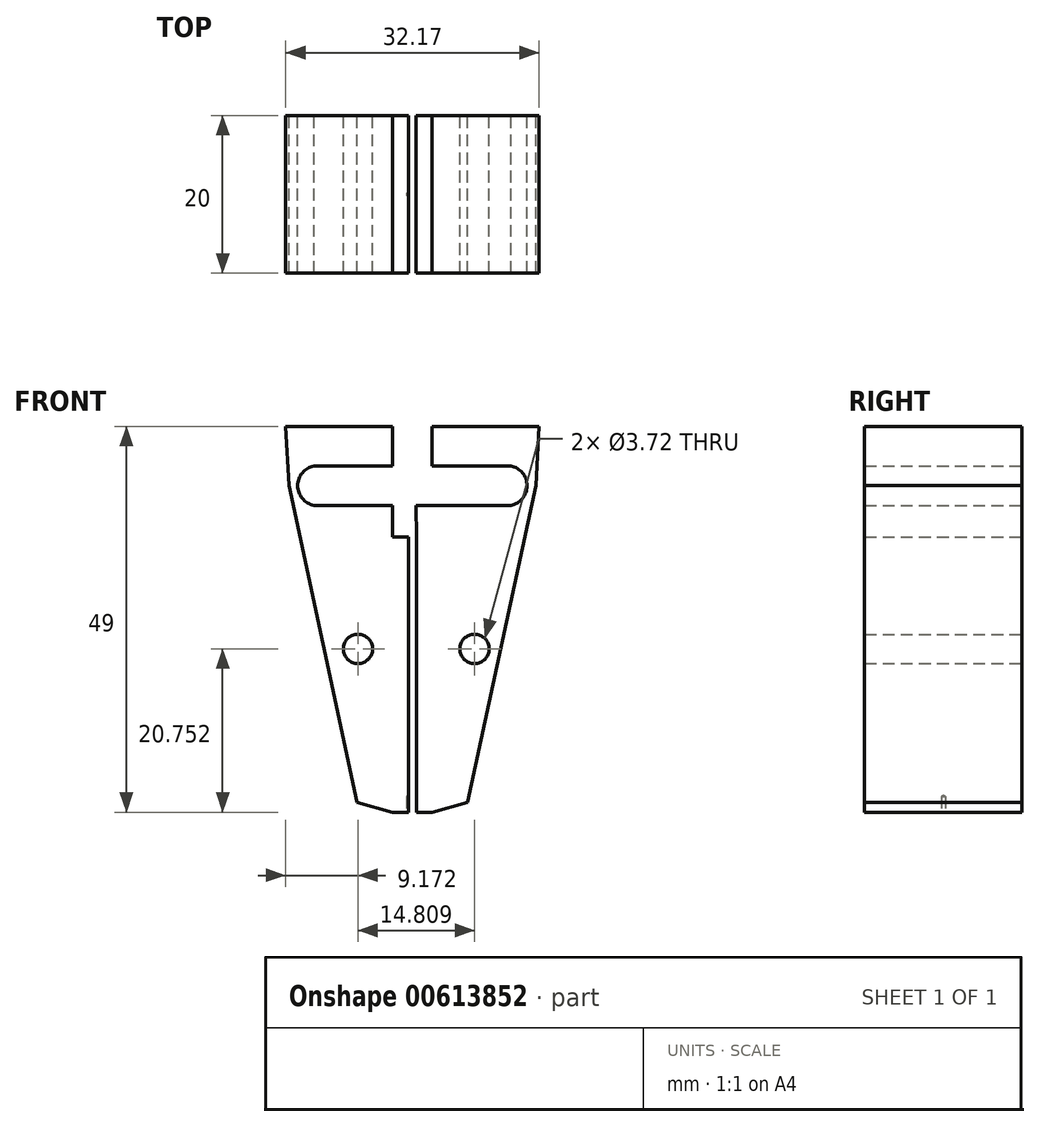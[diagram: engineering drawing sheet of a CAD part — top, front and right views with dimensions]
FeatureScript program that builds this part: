
annotation { "Feature Type Name" : "Feature", "Feature Type Description" : "" }
export const myFeature = defineFeature(function(context is Context, id is Id, definition is map)
    precondition{}
    {
        {
            var Q0;
            Q0=qCreatedBy(makeId("Front.planeOp"),FACE);
            var sketch = newSketch(context, id + "F0", { "sketchPlane" : qUnion([Q0])});
            skLineSegment(sketch, "E0.MirrorCS", {"start": v(38.69, 62.48) * mm, "end": v(39.08, 69.98) * mm});
            skLineSegment(sketch, "E1.MirrorCS", {"start": v(30.03, 22.23) * mm, "end": v(38.69, 62.48) * mm});
            skLineSegment(sketch, "E2.MirrorCS", {"start": v(25.5, 20.98) * mm, "end": v(30.03, 22.23) * mm});
            skLineSegment(sketch, "E3.MirrorCS", {"start": v(25.5, 64.98) * mm, "end": v(25.5, 69.98) * mm});
            skLineSegment(sketch, "E4.MirrorCS", {"start": v(35.5, 64.98) * mm, "end": v(25.5, 64.98) * mm});
            skArc(sketch, "E5.MirrorCS", {"start": v(35.5, 64.98) * mm, "mid": v(37.56, 62.48) * mm, "end": v(35.5, 59.98) * mm});
            skLineSegment(sketch, "E6.MirrorCS", {"start": v(25.5, 59.98) * mm, "end": v(35.5, 59.98) * mm});
            skLineSegment(sketch, "E7.MirrorCS", {"start": v(25.5, 20.98) * mm, "end": v(25.5, 55.9) * mm});
            skLineSegment(sketch, "E8", {"start": v(25.5, 69.98) * mm, "end": v(39.08, 69.98) * mm});
            skLineSegment(sketch, "E9.MirrorCS", {"start": v(20.5, 20.98) * mm, "end": v(20.5, 55.98) * mm});
            skLineSegment(sketch, "E10.MirrorCS", {"start": v(20.5, 59.98) * mm, "end": v(10.5, 59.98) * mm});
            skArc(sketch, "E11.MirrorCS", {"start": v(10.5, 64.98) * mm, "mid": v(8.43, 62.48) * mm, "end": v(10.5, 59.98) * mm});
            skLineSegment(sketch, "E12.MirrorCS", {"start": v(10.5, 64.98) * mm, "end": v(20.5, 64.98) * mm});
            skLineSegment(sketch, "E13.MirrorCS", {"start": v(20.5, 64.98) * mm, "end": v(20.5, 69.98) * mm});
            skLineSegment(sketch, "E14.MirrorCS", {"start": v(20.5, 69.98) * mm, "end": v(6.91, 69.98) * mm});
            skLineSegment(sketch, "E15.MirrorCS", {"start": v(7.3, 62.48) * mm, "end": v(6.91, 69.98) * mm});
            skLineSegment(sketch, "E16.MirrorCS", {"start": v(15.97, 22.23) * mm, "end": v(7.3, 62.48) * mm});
            skLineSegment(sketch, "E17.MirrorCS", {"start": v(20.5, 20.98) * mm, "end": v(15.97, 22.23) * mm});
            skLineSegment(sketch, "E18", {"start": v(10.98, 62.48) * mm, "end": v(35.02, 62.48) * mm, "construction": true});
            skLineSegment(sketch, "E19", {"start": v(74.89, 62.48) * mm, "end": v(35.02, 62.48) * mm, "construction": true});
            skLineSegment(sketch, "E20", {"start": v(10.98, 62.48) * mm, "end": v(-13.58, 62.48) * mm, "construction": true});
            skLineSegment(sketch, "E21.direction2", {"start": v(20.5, 22.1) * mm, "end": v(20.5, 24.4) * mm, "construction": true});
            skLineSegment(sketch, "E22", {"start": v(20.5, 64.98) * mm, "end": v(20.5, 59.98) * mm, "construction": true});
            skLineSegment(sketch, "E23", {"start": v(20.5, 59.98) * mm, "end": v(20.5, 55.98) * mm});
            skLineSegment(sketch, "E24", {"start": v(25.5, 59.98) * mm, "end": v(25.5, 55.9) * mm});
            skLineSegment(sketch, "E25", {"start": v(16.32, 40.5) * mm, "end": v(17.27, 35.55) * mm, "construction": true});
            skCircle(sketch, "E26", {"center": v(16.08, 41.73) * mm, "radius": 1.86 * mm});
            skLineSegment(sketch, "E27", {"start": v(20.5, 55.98) * mm, "end": v(22.5, 55.98) * mm});
            skLineSegment(sketch, "E28", {"start": v(22.5, 55.98) * mm, "end": v(22.5, 20.98) * mm});
            skLineSegment(sketch, "E29", {"start": v(22.5, 20.98) * mm, "end": v(20.5, 20.98) * mm});
            skLineSegment(sketch, "E30", {"start": v(25.5, 55.9) * mm, "end": v(23.5, 55.9) * mm});
            skLineSegment(sketch, "E31", {"start": v(23.5, 55.9) * mm, "end": v(23.5, 20.98) * mm});
            skLineSegment(sketch, "E32", {"start": v(23.5, 20.98) * mm, "end": v(25.5, 20.98) * mm});
            skLineSegment(sketch, "E33", {"start": v(10.5, 64.98) * mm, "end": v(10.98, 62.48) * mm, "construction": true});
            skLineSegment(sketch, "E34", {"start": v(10.5, 64.98) * mm, "end": v(17.27, 35.55) * mm, "construction": true});
            skLineSegment(sketch, "E35", {"start": v(23.49, 75.05) * mm, "end": v(23.49, 15.92) * mm});
            skCircle(sketch, "E36.MirrorC", {"center": v(30.9, 41.73) * mm, "radius": 1.86 * mm});
            skLineSegment(sketch, "E37", {"start": v(25.5, 59.98) * mm, "end": v(23.49, 59.98) * mm});
            skLineSegment(sketch, "E38", {"start": v(23.49, 59.98) * mm, "end": v(23.5, 55.9) * mm});
            skSolve(sketch);
        }
        {
            var Q0;
            Q0=makeQuery(id+"F0.imprint","IMPRINT",FACE,{"disambiguationData":[TD([[makeQuery(id+"F0.imprint","IMPRINT",EDGE,{"derivedFrom":sQuery(id+"F0.wireOp",EDGE,"E0.MirrorCS")}),1.0]])]});
            var Q1;
            Q1=makeQuery(id+"F0.imprint","IMPRINT",FACE,{"disambiguationData":[TD([[makeQuery(id+"F0.imprint","IMPRINT",EDGE,{"derivedFrom":sQuery(id+"F0.wireOp",EDGE,"E7.MirrorCS")}),1.0]])]});
            var Q2;
            Q2=makeQuery(id+"F0.imprint","IMPRINT",FACE,{"disambiguationData":[TD([[makeQuery(id+"F0.imprint","IMPRINT",EDGE,{"derivedFrom":sQuery(id+"F0.wireOp",EDGE,"E9.MirrorCS")}),-1.0]])]});
            var Q3;
            Q3=makeQuery(id+"F0.imprint","IMPRINT",FACE,{"disambiguationData":[TD([[makeQuery(id+"F0.imprint","IMPRINT",EDGE,{"derivedFrom":sQuery(id+"F0.wireOp",EDGE,"E9.MirrorCS")}),1.0]])]});
            var Q4;
            Q4=makeQuery(id+"F0.imprint","IMPRINT",FACE,{"disambiguationData":[TD([[makeQuery(id+"F0.imprint","IMPRINT",EDGE,{"derivedFrom":sQuery(id+"F0.wireOp",EDGE,"E24")}),-1.0]])]});
            extrude(context, id + "F1", {"entities" : qUnion([Q0, Q1, Q2, Q3, Q4]), "depth" : 20 * mm, "offsetDistance" : 25 * mm});
        }
        {
            var Q0;
            Q0=makeQuery(id+"F1.opExtrude","SWEPT_FACE",FACE,{"disambiguationData":[OSD([sQuery(id+"F0.wireOp",EDGE,"E29")])]});
            var sketch = newSketch(context, id + "F2", { "sketchPlane" : qUnion([Q0])});
            skArc(sketch, "E39", {"start": v(22.5, 10.4) * mm, "mid": v(22.1, 10) * mm, "end": v(22.5, 9.6) * mm});
            skSolve(sketch);
        }
        {
            var Q0;
            Q0=sQuery(id+"F2.wireOp",VERTEX,"E39.center");
            var Q1;
            Q1=makeQuery(id+"F1.opExtrude","SWEPT_BODY",BODY,{"disambiguationData":[OSD([sQuery(id+"F0.wireOp",EDGE,"E10.MirrorCS"),sQuery(id+"F0.wireOp",EDGE,"E11.MirrorCS"),sQuery(id+"F0.wireOp",EDGE,"E12.MirrorCS"),sQuery(id+"F0.wireOp",EDGE,"E13.MirrorCS"),sQuery(id+"F0.wireOp",EDGE,"E14.MirrorCS"),sQuery(id+"F0.wireOp",EDGE,"E15.MirrorCS"),sQuery(id+"F0.wireOp",EDGE,"E16.MirrorCS"),sQuery(id+"F0.wireOp",EDGE,"E17.MirrorCS"),sQuery(id+"F0.wireOp",EDGE,"E23"),sQuery(id+"F0.wireOp",EDGE,"E26"),sQuery(id+"F0.wireOp",EDGE,"E27"),sQuery(id+"F0.wireOp",EDGE,"E28"),sQuery(id+"F0.wireOp",EDGE,"E29")])]});
            hole(context, id + "F3", {"style" : HoleStyle.SIMPLE, "endStyle" : HoleEndStyle.BLIND, "holeDiameter" : 0.5 * mm, "majorDiameter" : 5 * mm, "holeDepth" : 2 * mm, "isTappedThrough" : true, "tappedDepth" : 12 * mm, "tapClearance" : 3, "startFromSketch" : true, "locations" : qUnion([Q0]), "scope" : qUnion([Q1])});
        }
    });
